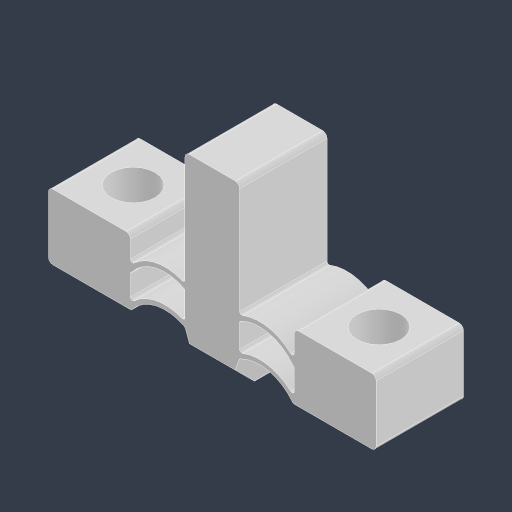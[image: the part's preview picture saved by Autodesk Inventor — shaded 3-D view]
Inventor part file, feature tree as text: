
AUTODESK INVENTOR PART (.ipt)
format: ipt  version: 2023.4 (Build 274418000, 418)  size: 219,136 bytes
history: native  units: mm
features: chamfer x2, fillet x2, sketch x2, extrude x1, hole x1
ambient origin geometry x8: Origin, YZ Plane, XZ Plane, XY Plane, X Axis, Y Axis, Z Axis, Center Point
bodies: Solid1 (feature_tree)
feature tree (8):
  extrude  "Extrusion1"  Depth=18.0mm
  chamfer  "Chamfer1"  Distance=3.0mm
  chamfer  "Chamfer2"  Distance=3.0mm
  fillet  "Fillet1"  Radius=5.0mm
  fillet  "Fillet2"  Radius=9.0mm
  hole  "Hole2"  [1 undecoded]
  sketch  "Sketch1"  dims[d0=5.0mm d1=18.0mm]
  sketch  "Sketch3"  dims[d2=30.0mm d3=3.0mm d4=3.0mm d5=5.0mm d8=9.0mm d9=3.0mm d10=2.0mm d11=3.490659mm d12=0.4mm d13=4.0mm d14=3.0mm d15=8.0mm d16=0.0mm d25=3.0mm d26=2.0mm d27=45.0deg d28=3.0mm d29=2.0mm d30=45.0deg d31=0.2mm d32=0.4mm d34=4.0mm d35=6.0mm d36=4.0mm d37=2.0mm d38=90.0deg d39=8.0mm d40=20.594885mm]
note: 1 required parameter value undecoded (feature->parameter linkage not recoverable at this tier; creation-order binding heuristic only, values carry confidence <= 0.55)
